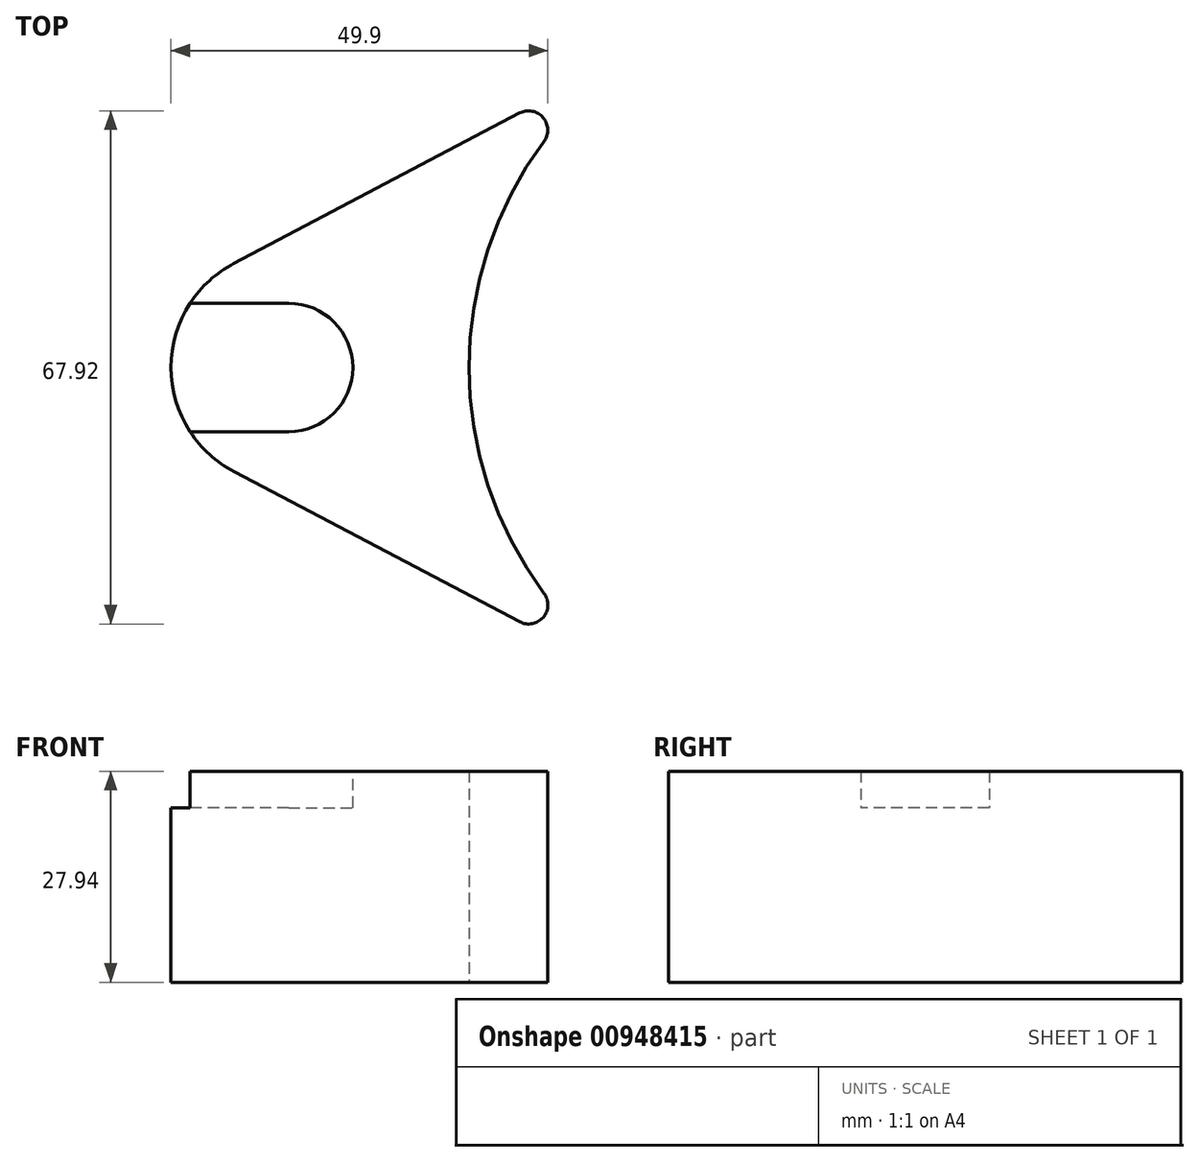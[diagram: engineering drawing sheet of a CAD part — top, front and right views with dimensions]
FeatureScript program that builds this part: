
annotation { "Feature Type Name" : "Feature", "Feature Type Description" : "" }
export const myFeature = defineFeature(function(context is Context, id is Id, definition is map)
    precondition{}
    {
        {
            var Q0;
            Q0=qCreatedBy(makeId("Top.planeOp"),FACE);
            var sketch = newSketch(context, id + "F0", { "sketchPlane" : qUnion([Q0])});
            skArc(sketch, "E0", {"start": v(-25.23, 43.16) * mm, "mid": v(-50, -0.01) * mm, "end": v(-25.21, -43.17) * mm});
            skPoint(sketch, "E1.first.point", {"position": v(-79.3, 6.23) * mm});
            skPoint(sketch, "E1.second.point", {"position": v(-76.8, -7.76) * mm});
            skPoint(sketch, "E1.third.point", {"position": v(-66.58, 3.83) * mm});
            skPoint(sketch, "E2", {"position": v(-73.9, -0.02) * mm});
            skArc(sketch, "E3", {"start": v(-81.14, 13.75) * mm, "mid": v(-89.45, -0.02) * mm, "end": v(-81.13, -13.8) * mm});
            skLineSegment(sketch, "E4", {"start": v(-25.21, -43.17) * mm, "end": v(-81.13, -13.8) * mm});
            skLineSegment(sketch, "E5", {"start": v(-73.9, -0.02) * mm, "end": v(0, 0) * mm, "construction": true});
            skLineSegment(sketch, "E6.MirrorCS", {"start": v(-25.23, 43.16) * mm, "end": v(-81.14, 13.75) * mm});
            skSolve(sketch);
        }
        {
            var Q0;
            Q0 = qSketchRegion(id + "F0", true);
            extrude(context, id + "F1", {"entities" : qUnion([Q0]), "depth" : 27.94 * mm, "offsetDistance" : 25.4 * mm});
        }
        {
            var Q0;
            Q0=makeQuery(id+"F1.opExtrude","CAP_FACE",FACE,{"disambiguationData":[OSD([sQuery(id+"F0.wireOp",EDGE,"E0"),sQuery(id+"F0.wireOp",EDGE,"E3"),sQuery(id+"F0.wireOp",EDGE,"E4"),sQuery(id+"F0.wireOp",EDGE,"E6.MirrorCS")])],"isStart":false});
            var sketch = newSketch(context, id + "F2", { "sketchPlane" : qUnion([Q0])});
            skArc(sketch, "E7", {"start": v(-73.9, -8.53) * mm, "mid": v(-65.39, -0.02) * mm, "end": v(-73.9, 8.49) * mm});
            skLineSegment(sketch, "E8", {"start": v(-73.9, 8.49) * mm, "end": v(-73.9, -8.53) * mm, "construction": true});
            skLineSegment(sketch, "E9.bottom", {"start": v(-73.9, 8.49) * mm, "end": v(-100.94, 8.49) * mm});
            skLineSegment(sketch, "E9.top", {"start": v(-73.9, -8.53) * mm, "end": v(-100.94, -8.53) * mm});
            skLineSegment(sketch, "E9.left", {"start": v(-73.9, 8.49) * mm, "end": v(-73.9, -8.53) * mm});
            skLineSegment(sketch, "E9.right", {"start": v(-100.94, 8.49) * mm, "end": v(-100.94, -8.53) * mm});
            skSolve(sketch);
        }
        {
            var Q0;
            Q0 = qSketchRegion(id + "F2", true);
            extrude(context, id + "F3", {"entities" : qUnion([Q0]), "operationType" : NewBodyOperationType.REMOVE, "oppositeDirection" : true, "depth" : 4.83 * mm, "offsetDistance" : 25.4 * mm});
        }
        {
            var Q0;
            Q0=makeQuery(id+"F1.opExtrude","SWEPT_EDGE",EDGE,{"disambiguationData":[OSD([sQuery(id+"F0.wireOp",EDGE,"E0"),sQuery(id+"F0.wireOp",EDGE,"E4")])]});
            var Q1;
            Q1=makeQuery(id+"F1.opExtrude","SWEPT_EDGE",EDGE,{"disambiguationData":[OSD([sQuery(id+"F0.wireOp",EDGE,"E0"),sQuery(id+"F0.wireOp",EDGE,"E6.MirrorCS")])]});
            fillet(context, id + "F4", {"entities" : qUnion([Q0, Q1]), "radius" : 2.54 * mm, "tangentPropagation" : true, "allowEdgeOverflow" : false});
        }
    });
